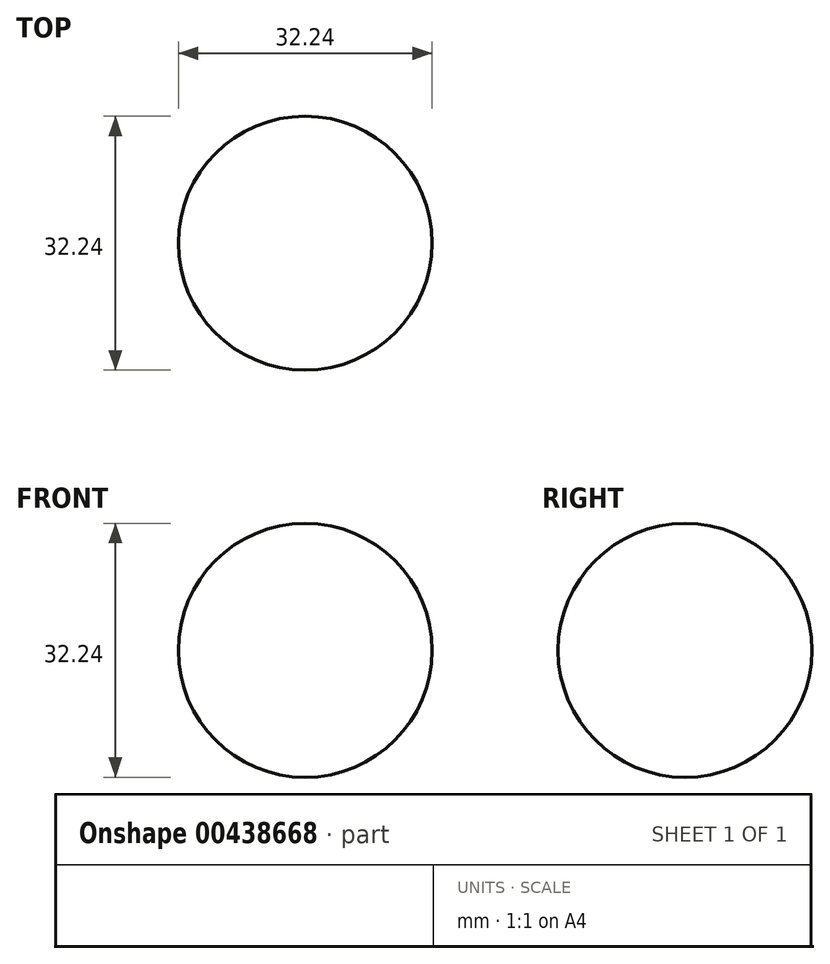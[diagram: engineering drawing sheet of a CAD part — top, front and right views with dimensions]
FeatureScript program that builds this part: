
annotation { "Feature Type Name" : "Feature", "Feature Type Description" : "" }
export const myFeature = defineFeature(function(context is Context, id is Id, definition is map)
    precondition{}
    {
        {
            var Q0;
            Q0=qCreatedBy(makeId("Front.planeOp"),FACE);
            var sketch = newSketch(context, id + "F0", { "sketchPlane" : qUnion([Q0])});
            skArc(sketch, "E0", {"start": v(0, 16.12) * mm, "mid": v(-16.12, 0) * mm, "end": v(0, -16.12) * mm});
            skFitSpline(sketch, "E1", {"points": [v(-24.53, -14.12) * mm, v(-32.38, 45.29) * mm, v(-26.12, 55.66) * mm, v(-16.73, 55.46) * mm, v(-16.37, 10.23) * mm], "startDerivative": vector(-39.08, 192.43) * mm, "endDerivative": vector(-22.89, -187.04) * mm});
            skArc(sketch, "E2", {"start": v(-16.37, -10.23) * mm, "mid": v(-9.5, -16.2) * mm, "end": v(-0.54, -17.75) * mm});
            skPoint(sketch, "E3.orphan", {"position": v(-7.73, -17.68) * mm});
            skArc(sketch, "E4", {"start": v(-17.06, 9.02) * mm, "mid": v(-19.28, -0.7) * mm, "end": v(-16.37, -10.23) * mm});
            skArc(sketch, "E5", {"start": v(0.64, -19.05) * mm, "mid": v(0.5, -18.63) * mm, "end": v(0.33, -18.22) * mm});
            skArc(sketch, "E6", {"start": v(-22.06, -15.62) * mm, "mid": v(-11.44, -19.55) * mm, "end": v(-0.12, -20.14) * mm});
            skPoint(sketch, "E7.orphan", {"position": v(0, -22.44) * mm});
            skArc(sketch, "E8.filletArc", {"start": v(-22.47, -15.37) * mm, "mid": v(-22.27, -15.5) * mm, "end": v(-22.06, -15.62) * mm});
            skPoint(sketch, "E9.visualSharp", {"position": v(0.77, -20.04) * mm});
            skArc(sketch, "E9.filletArc", {"start": v(-0.12, -20.14) * mm, "mid": v(0.51, -19.77) * mm, "end": v(0.64, -19.05) * mm});
            skPoint(sketch, "E10.visualSharp", {"position": v(0, -17.68) * mm});
            skArc(sketch, "E10.filletArc", {"start": v(0.33, -18.22) * mm, "mid": v(-0.03, -17.85) * mm, "end": v(-0.54, -17.75) * mm});
            skCircle(sketch, "E11", {"center": v(-23.02, 46.96) * mm, "radius": 4.58 * mm});
            skFitSpline(sketch, "E12", {"points": [v(-32.38, 45.29) * mm, v(-25.2, -11.34) * mm, v(-6.92, -31.12) * mm], "startDerivative": vector(2.38, -109.44) * mm, "endDerivative": vector(51.59, -39.01) * mm});
            skArc(sketch, "E13.filletArc", {"start": v(-17.06, 9.02) * mm, "mid": v(-16.48, 10.4) * mm, "end": v(-16.16, 11.88) * mm});
            skFitSpline(sketch, "E14", {"points": [v(-27.06, -6.65) * mm, v(-22.06, -15.62) * mm, v(9.44, -14.46) * mm], "startDerivative": vector(7.16, -29.54) * mm, "endDerivative": vector(60.88, 10.26) * mm});
            skPoint(sketch, "E15.orphan", {"position": v(-23.56, -14.46) * mm});
            skLineSegment(sketch, "E16", {"start": v(0, 16.12) * mm, "end": v(0, 24.89) * mm});
            skLineSegment(sketch, "E17", {"start": v(0, 16.12) * mm, "end": v(0, -16.12) * mm});
            skSolve(sketch);
        }
        {
            var Q0;
            Q0=makeQuery(id+"F0.imprint","IMPRINT",FACE,{"disambiguationData":[TD([[makeQuery(id+"F0.imprint","IMPRINT",EDGE,{"derivedFrom":sQuery(id+"F0.wireOp",EDGE,"E0")}),1.0]])]});
            var Q1;
            Q1=sQuery(id+"F0.wireOp",EDGE,"E16");
            revolve(context, id + "F1", {"entities" : qUnion([Q0]), "axis" : qUnion([Q1]), "revolveType" : RevolveType.FULL});
        }
    });
